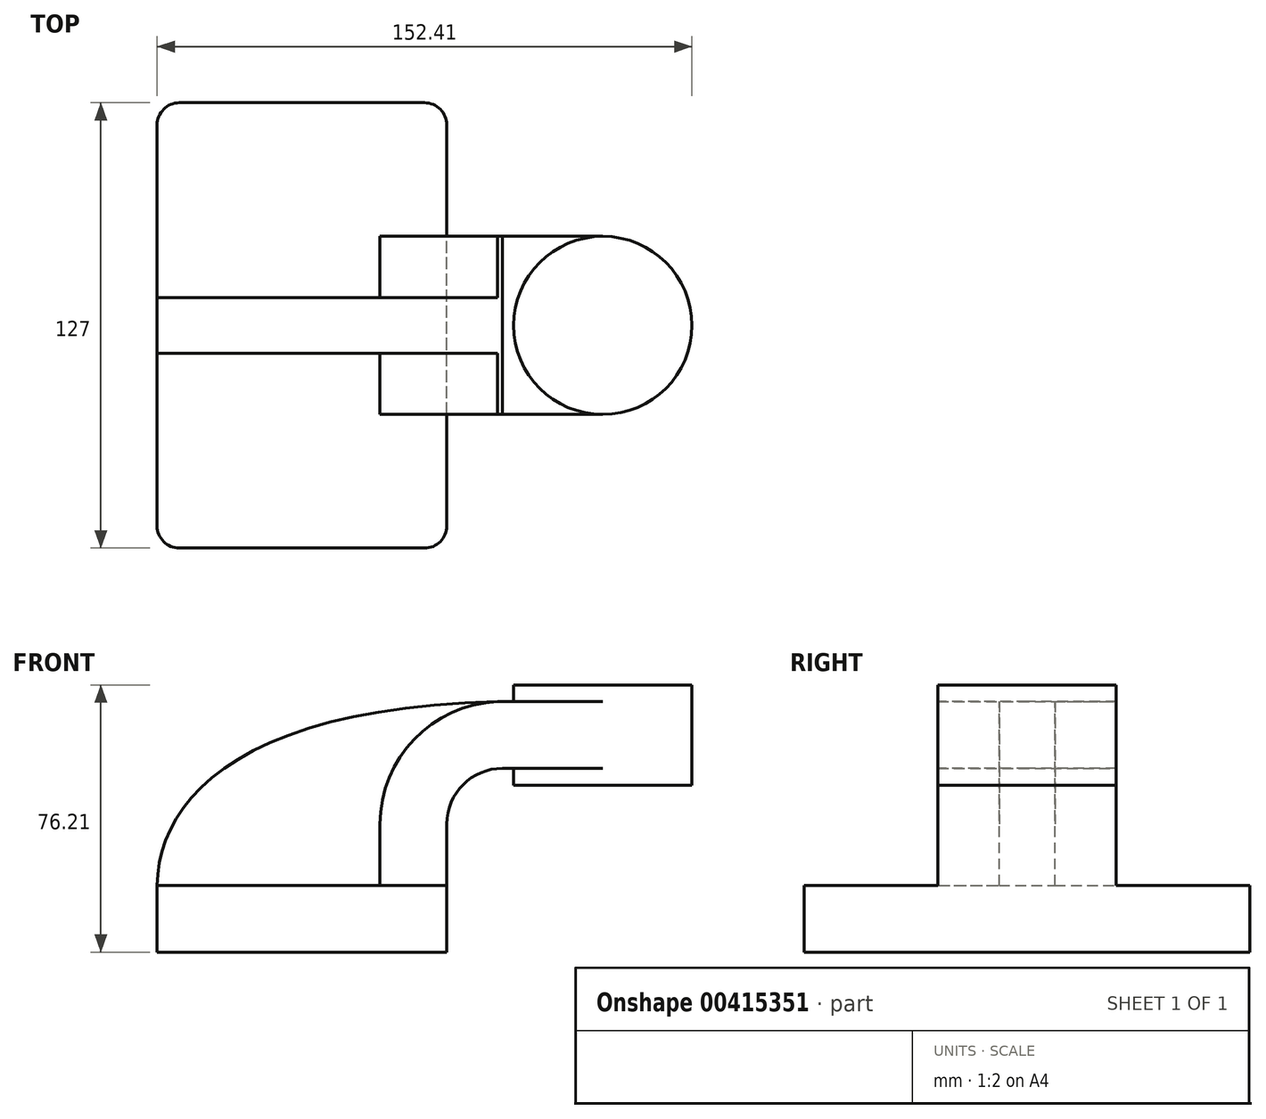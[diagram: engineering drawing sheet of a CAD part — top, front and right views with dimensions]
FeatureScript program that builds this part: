
annotation { "Feature Type Name" : "Feature", "Feature Type Description" : "" }
export const myFeature = defineFeature(function(context is Context, id is Id, definition is map)
    precondition{}
    {
        {
            var Q0;
            Q0=qCreatedBy(makeId("Front.planeOp"),FACE);
            var sketch = newSketch(context, id + "F0", { "sketchPlane" : qUnion([Q0])});
            skLineSegment(sketch, "E0.bottom", {"start": v(-41.27, -9.53) * mm, "end": v(41.28, -9.53) * mm});
            skLineSegment(sketch, "E0.top", {"start": v(-41.28, 9.53) * mm, "end": v(41.28, 9.53) * mm});
            skLineSegment(sketch, "E0.left", {"start": v(-41.28, -9.53) * mm, "end": v(-41.28, 9.53) * mm});
            skLineSegment(sketch, "E0.right", {"start": v(41.28, -9.53) * mm, "end": v(41.28, 9.53) * mm});
            skPoint(sketch, "E0.middle", {"position": v(0, 0) * mm});
            skLineSegment(sketch, "E1.bottom", {"start": v(60.32, 38.1) * mm, "end": v(111.12, 38.1) * mm});
            skLineSegment(sketch, "E1.top", {"start": v(60.32, 66.67) * mm, "end": v(111.12, 66.67) * mm});
            skLineSegment(sketch, "E1.left", {"start": v(60.32, 38.1) * mm, "end": v(60.32, 66.67) * mm});
            skLineSegment(sketch, "E1.right", {"start": v(111.12, 38.1) * mm, "end": v(111.12, 66.67) * mm});
            skPoint(sketch, "E1.middle", {"position": v(85.72, 52.39) * mm});
            skLineSegment(sketch, "E2", {"start": v(41.28, 9.53) * mm, "end": v(41.28, 27) * mm});
            skArc(sketch, "E3", {"start": v(41.27, 27) * mm, "mid": v(45.92, 38.23) * mm, "end": v(57.15, 42.88) * mm});
            skLineSegment(sketch, "E4", {"start": v(57.15, 42.88) * mm, "end": v(85.72, 42.88) * mm});
            skLineSegment(sketch, "E5.0", {"start": v(57.15, 61.93) * mm, "end": v(85.72, 61.93) * mm});
            skArc(sketch, "E5.1", {"start": v(22.22, 27) * mm, "mid": v(32.45, 51.7) * mm, "end": v(57.15, 61.93) * mm});
            skLineSegment(sketch, "E5.2", {"start": v(22.22, 9.53) * mm, "end": v(22.22, 27) * mm});
            skLineSegment(sketch, "E6", {"start": v(85.72, 42.88) * mm, "end": v(85.72, 61.93) * mm});
            skFitSpline(sketch, "E7", {"points": [v(-41.27, 9.52) * mm, v(57.15, 61.93) * mm], "startDerivative": vector(0.84, 73.43) * mm, "endDerivative": vector(223.6, 4.07) * mm});
            skLineSegment(sketch, "E8", {"start": v(85.72, 61.93) * mm, "end": v(85.72, 66.67) * mm});
            skLineSegment(sketch, "E9", {"start": v(85.72, 42.88) * mm, "end": v(85.72, 38.1) * mm});
            skSolve(sketch);
        }
        {
            var Q0;
            Q0=makeQuery(id+"F0.imprint","IMPRINT",FACE,{"disambiguationData":[TD([[makeQuery(id+"F0.imprint","IMPRINT",EDGE,{"derivedFrom":sQuery(id+"F0.wireOp",EDGE,"E0.bottom")}),1.0]])]});
            extrude(context, id + "F1", {"entities" : qUnion([Q0]), "endBound" : BoundingType.SYMMETRIC, "depth" : 127 * mm});
        }
        {
            var Q0;
            {var subQ0=sQuery(id+"F0.wireOp",EDGE,"E2");Q0=makeQuery(id+"F0.imprint","IMPRINT",FACE,{"disambiguationData":[TD([[makeQuery(id+"F0.imprint","IMPRINT",EDGE,{"derivedFrom":subQ0}),1.0]])]});}
            var Q1;
            {var subQ5=sQuery(id+"F0.wireOp",EDGE,"E6");Q1=makeQuery(id+"F0.imprint","IMPRINT",FACE,{"disambiguationData":[TD([[makeQuery(id+"F0.imprint","IMPRINT",EDGE,{"derivedFrom":subQ5}),1.0]])]});}
            extrude(context, id + "F2", {"entities" : qUnion([Q0, Q1]), "operationType" : NewBodyOperationType.ADD, "endBound" : BoundingType.SYMMETRIC, "depth" : 50.8 * mm});
        }
        {
            var Q0;
            {var subQ3=sQuery(id+"F0.wireOp",EDGE,"E5.2");Q0=makeQuery(id+"F0.imprint","IMPRINT",FACE,{"disambiguationData":[TD([[makeQuery(id+"F0.imprint","IMPRINT",EDGE,{"derivedFrom":subQ3}),1.0]])]});}
            extrude(context, id + "F3", {"entities" : qUnion([Q0]), "operationType" : NewBodyOperationType.ADD, "endBound" : BoundingType.SYMMETRIC, "depth" : 15.88 * mm});
        }
        {
            var Q0;
            {var subQ0=sQuery(id+"F0.wireOp",EDGE,"E1.right");Q0=makeQuery(id+"F0.imprint","IMPRINT",FACE,{"disambiguationData":[TD([[makeQuery(id+"F0.imprint","IMPRINT",EDGE,{"derivedFrom":subQ0}),1.0]])]});}
            var Q1;
            Q1=sQuery(id+"F0.wireOp",EDGE,"E8");
            revolve(context, id + "F4", {"operationType" : NewBodyOperationType.ADD, "entities" : qUnion([Q0]), "axis" : qUnion([Q1]), "revolveType" : RevolveType.FULL});
        }
        {
            var Q0;
            Q0=makeQuery(id+"F1.opExtrude","CAP_EDGE",EDGE,{"disambiguationData":[OSD([sQuery(id+"F0.wireOp",EDGE,"E0.right")])],"isStart":false});
            var Q1;
            Q1=makeQuery(id+"F1.opExtrude","CAP_EDGE",EDGE,{"disambiguationData":[OSD([sQuery(id+"F0.wireOp",EDGE,"E0.left")])],"isStart":false});
            var Q2;
            Q2=makeQuery(id+"F1.opExtrude","CAP_EDGE",EDGE,{"disambiguationData":[OSD([sQuery(id+"F0.wireOp",EDGE,"E0.right")])],"isStart":true});
            var Q3;
            Q3=makeQuery(id+"F1.opExtrude","CAP_EDGE",EDGE,{"disambiguationData":[OSD([sQuery(id+"F0.wireOp",EDGE,"E0.left")])],"isStart":true});
            fillet(context, id + "F5", {"entities" : qUnion([Q0, Q1, Q2, Q3]), "radius" : 6.35 * mm, "tangentPropagation" : true, "allowEdgeOverflow" : false});
        }
    });
